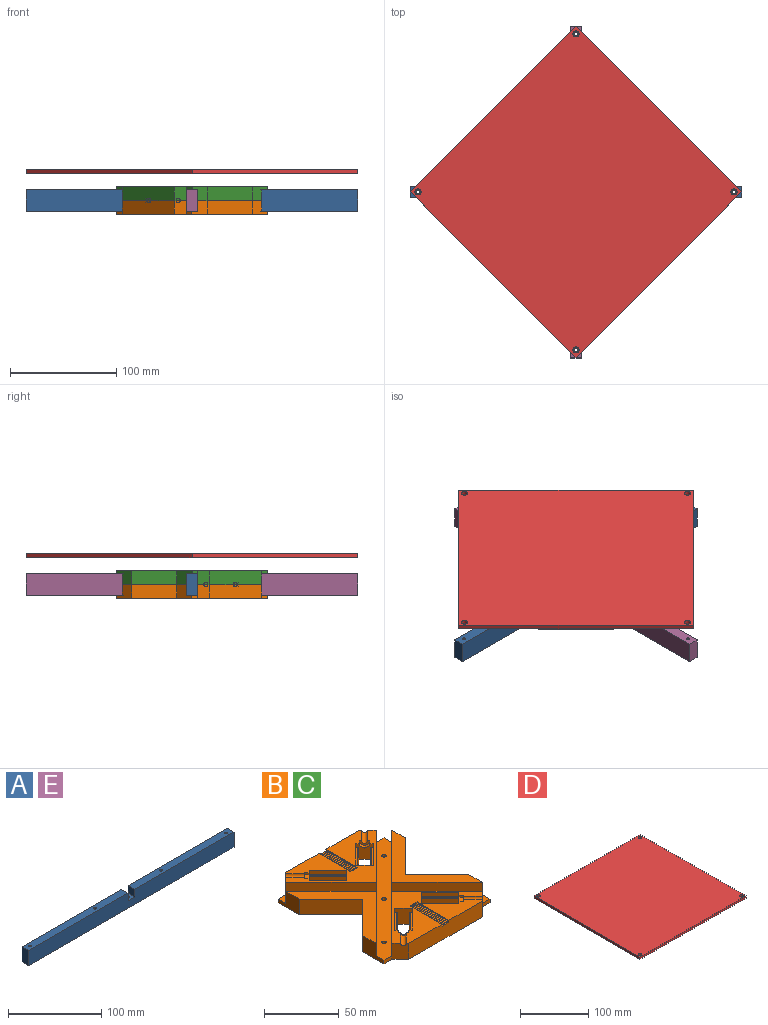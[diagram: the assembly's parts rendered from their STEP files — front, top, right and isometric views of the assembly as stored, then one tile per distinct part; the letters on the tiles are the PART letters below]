
ASSEMBLY  parts=5 mates=6
PART A: 15 faces, bbox 312x10x20 mm
  f0: plane 151x10mm, normal (0,0,1), area 1495.9mm2, adj f2,f3,f4,f7,f10,f14
  f1: cylinder r=1.5mm len=10mm, axis (0,0,-1), area 94.2mm2, adj f9,f12
  f2: plane 312x20mm, normal (0,-1,0), area 6140mm2, adj f0,f3,f5,f8,f9,f10,f11,f12
  f3: plane 20x10mm, normal (1,0,0), area 200mm2, adj f0,f2,f4,f9
  f4: plane 312x20mm, normal (0,1,0), area 6140mm2, adj f0,f3,f5,f8,f9,f10,f11,f12
  f5: plane 20x10mm, normal (-1,0,0), area 200mm2, adj f2,f4,f8,f9
  f6: cylinder r=1.5mm len=20mm, axis (0,0,-1), area 188.5mm2, adj f8,f9
  f7: cylinder r=1.5mm len=20mm, axis (0,0,-1), area 188.5mm2, adj f0,f9
  f8: plane 151x10mm, normal (0,0,1), area 1495.9mm2, adj f2,f4,f5,f6,f11,f13
  f9: plane 312x10mm, normal (0,0,-1), area 3084.7mm2, adj f1,f2,f3,f4,f5,f6,f7,f13
  f10: plane 10x10mm, normal (-1,0,0), area 100mm2, adj f0,f2,f4,f12
  f11: plane 10x10mm, normal (1,0,0), area 100mm2, adj f2,f4,f8,f12
  f12: plane 10x10mm, normal (0,0,1), area 92.9mm2, adj f1,f2,f4,f10,f11
  f13: cylinder r=1.5mm len=20mm, axis (0,0,1), area 188.5mm2, adj f8,f9
  f14: cylinder r=1.5mm len=20mm, axis (0,0,1), area 188.5mm2, adj f0,f9
PART B: 227 faces, bbox 100x116x13 mm
  f0: plane 6.5x0.5mm, normal (0,0,1), area 3.3mm2, adj f106,f107,f108,f198
  f1: plane 69.29x13mm, normal (0,1,0), area 890.7mm2, adj f5,f17,f48,f49,f106,f107,f154
  f2: plane 6.5x0.5mm, normal (0,0,1), area 3.3mm2, adj f103,f104,f105,f213
  f3: plane 69.29x13mm, normal (0,-1,0), area 890.7mm2, adj f4,f17,f46,f47,f103,f105,f110
  f4: plane 85.29x50.65mm, normal (0,0,1), area 1500.1mm2, adj f3,f6,f40,f41,f46,f47,f50,f51
  f5: plane 85.29x50.65mm, normal (0,0,1), area 1500.1mm2, adj f1,f7,f8,f38,f39,f48,f49,f53
  f6: plane 13x8.49mm, normal (0.71,0.71,0), area 95.6mm2, adj f4,f9,f10,f17,f67,f68,f69,f70
  f7: plane 13x8.49mm, normal (0.71,-0.71,0), area 95.6mm2, adj f5,f15,f16,f17,f55,f56,f57,f58
  f8: plane 13x8.49mm, normal (-0.71,-0.71,0), area 95.6mm2, adj f5,f13,f14,f17,f59,f60,f61,f62
  f9: plane 17.68x17.68mm, normal (0.71,-0.71,0), area 240mm2, adj f6,f17,f50,f95
  f10: plane 17.68x17.68mm, normal (-0.71,0.71,0), area 240mm2, adj f6,f17,f50,f96
  f11: plane 17.68x17.68mm, normal (-0.71,-0.71,0), area 240mm2, adj f17,f51,f52,f97
  f12: plane 17.68x17.68mm, normal (0.71,0.71,0), area 240mm2, adj f17,f51,f52,f98
  f13: plane 17.68x17.68mm, normal (-0.71,0.71,0), area 240mm2, adj f8,f17,f53,f99
  f14: plane 17.68x17.68mm, normal (0.71,-0.71,0), area 240mm2, adj f8,f17,f53,f100
  f15: plane 17.68x17.68mm, normal (0.71,0.71,0), area 240mm2, adj f7,f17,f54,f101
  f16: plane 17.68x17.68mm, normal (-0.71,-0.71,0), area 240mm2, adj f7,f17,f54,f102
  f17: plane 116x100mm, normal (0,0,-1), area 8601.3mm2, adj f1,f3,f6,f7,f8,f9,f10,f11
  f18: plane 20x13mm, normal (1,0,0), area 186.5mm2, adj f17,f21,f23,f36,f37,f43
  f19: plane 20x13mm, normal (-1,0,0), area 186.5mm2, adj f17,f20,f23,f28,f33,f45
  f20: plane 85.29x42.65mm, normal (0,0,1), area 918.7mm2, adj f19,f26,f33,f34,f44,f45
  f21: plane 7.35x3mm, normal (0,-1,0), area 22.1mm2, adj f17,f18,f23,f46
  f22: plane 7.35x3mm, normal (0,1,0), area 22.1mm2, adj f17,f23,f24,f48
  f23: plane 100x100mm, normal (0,0,1), area 2689.9mm2, adj f18,f19,f21,f22,f24,f25,f26,f27
  f24: plane 20x13mm, normal (1,0,0), area 186.5mm2, adj f17,f22,f23,f35,f37,f42
  f25: plane 7.35x3mm, normal (0,1,0), area 22.1mm2, adj f17,f23,f26,f49
  f26: plane 20x13mm, normal (-1,0,0), area 186.5mm2, adj f17,f20,f23,f25,f34,f44
  f27: cylinder r=1.5mm len=3mm, axis (0,0,-1), area 28.3mm2, adj f17,f23
  f28: plane 7.35x3mm, normal (0,-1,0), area 22.1mm2, adj f17,f19,f23,f47
  f29: cylinder r=1.5mm len=3mm, axis (0,0,-1), area 28.3mm2, adj f17,f23
  f30: cylinder r=1.5mm len=3mm, axis (0,0,-1), area 28.3mm2, adj f17,f23
  f31: cylinder r=1.5mm len=3mm, axis (0,0,-1), area 28.3mm2, adj f17,f23
  f32: cylinder r=1.5mm len=3mm, axis (0,0,-1), area 28.3mm2, adj f17,f23
  f33: plane 42.65x42.65mm, normal (0.71,-0.71,0), area 603.1mm2, adj f19,f20,f23,f34
  f34: plane 42.65x42.65mm, normal (0.71,0.71,0), area 603.1mm2, adj f20,f23,f26,f33
  f35: plane 42.65x42.65mm, normal (-0.71,0.71,0), area 603.1mm2, adj f23,f24,f36,f37
  f36: plane 42.65x42.65mm, normal (-0.71,-0.71,0), area 603.1mm2, adj f18,f23,f35,f37
  f37: plane 85.29x42.65mm, normal (0,0,1), area 918.7mm2, adj f18,f24,f35,f36,f42,f43
  f38: plane 42.65x42.65mm, normal (-0.71,-0.71,0), area 603.1mm2, adj f5,f23,f39,f49
  f39: plane 42.65x42.65mm, normal (0.71,-0.71,0), area 603.1mm2, adj f5,f23,f38,f48
  f40: plane 42.65x42.65mm, normal (0.71,0.71,0), area 603.1mm2, adj f4,f23,f41,f46
  f41: plane 42.65x42.65mm, normal (-0.71,0.71,0), area 603.1mm2, adj f4,f23,f40,f47
  f42: plane 30x30mm, normal (0.71,-0.71,0), area 551.5mm2, adj f17,f24,f37,f43
  f43: plane 30x30mm, normal (0.71,0.71,0), area 551.5mm2, adj f17,f18,f37,f42
  f44: plane 30x30mm, normal (-0.71,-0.71,0), area 551.5mm2, adj f17,f20,f26,f45
  f45: plane 30x30mm, normal (-0.71,0.71,0), area 551.5mm2, adj f17,f19,f20,f44
  f46: plane 13x8mm, normal (0.71,-0.71,0), area 140.8mm2, adj f3,f4,f17,f21,f40,f94
  f47: plane 13x8mm, normal (-0.71,-0.71,0), area 140.8mm2, adj f3,f4,f17,f28,f41,f93
  f48: plane 13x8mm, normal (0.71,0.71,0), area 140.8mm2, adj f1,f5,f17,f22,f39,f91
  f49: plane 13x8mm, normal (-0.71,0.71,0), area 140.8mm2, adj f1,f5,f17,f25,f38,f92
  f50: plane 13x8.49mm, normal (-0.71,-0.71,0), area 116.1mm2, adj f4,f9,f10,f17,f67,f68,f69,f70
  f51: plane 13x8.49mm, normal (0.71,-0.71,0), area 116.1mm2, adj f4,f11,f12,f17,f63,f64,f65,f66
  f52: plane 13x8.49mm, normal (-0.71,0.71,0), area 95.6mm2, adj f4,f11,f12,f17,f63,f64,f65,f66
  f53: plane 13x8.49mm, normal (0.71,0.71,0), area 116.1mm2, adj f5,f13,f14,f17,f59,f60,f61,f62
  f54: plane 13x8.49mm, normal (-0.71,0.71,0), area 116.1mm2, adj f5,f15,f16,f17,f55,f56,f57,f58
  f55: plane 18.81x18.81mm, normal (0,0,1), area 40mm2, adj f7,f54,f56,f102
  f56: plane 17.68x17.68mm, normal (-0.71,-0.71,0), area 75mm2, adj f5,f7,f54,f55
  f57: plane 18.81x18.81mm, normal (0,0,1), area 40mm2, adj f7,f54,f58,f101
  f58: plane 17.68x17.68mm, normal (0.71,0.71,0), area 75mm2, adj f5,f7,f54,f57
  f59: plane 18.81x18.81mm, normal (0,0,1), area 40mm2, adj f8,f53,f60,f100
  f60: plane 17.68x17.68mm, normal (0.71,-0.71,0), area 75mm2, adj f5,f8,f53,f59
  f61: plane 18.81x18.81mm, normal (0,0,1), area 40mm2, adj f8,f53,f62,f99
  f62: plane 17.68x17.68mm, normal (-0.71,0.71,0), area 75mm2, adj f5,f8,f53,f61
  f63: plane 18.81x18.81mm, normal (0,0,1), area 40mm2, adj f51,f52,f64,f98
  f64: plane 17.68x17.68mm, normal (0.71,0.71,0), area 75mm2, adj f4,f51,f52,f63
  f65: plane 18.81x18.81mm, normal (0,0,1), area 40mm2, adj f51,f52,f66,f97
  f66: plane 17.68x17.68mm, normal (-0.71,-0.71,0), area 75mm2, adj f4,f51,f52,f65
  f67: plane 18.81x18.81mm, normal (0,0,1), area 40mm2, adj f6,f50,f68,f96
  f68: plane 17.68x17.68mm, normal (-0.71,0.71,0), area 75mm2, adj f4,f6,f50,f67
  f69: plane 18.81x18.81mm, normal (0,0,1), area 40mm2, adj f6,f50,f70,f95
  f70: plane 17.68x17.68mm, normal (0.71,-0.71,0), area 75mm2, adj f4,f6,f50,f69
  f71: plane 2.19x2.19mm, normal (0.71,-0.71,0), area 6.2mm2, adj f5,f8,f72,f75
  f72: plane 4.62x4.62mm, normal (0.35,-0.35,0.87), area 12.3mm2, adj f8,f71,f73,f75
  f73: plane 4.62x4.62mm, normal (-0.35,0.35,0.87), area 12.3mm2, adj f8,f72,f74,f75
  f74: plane 2.19x2.19mm, normal (-0.71,0.71,0), area 6.2mm2, adj f5,f8,f73,f75
  f75: plane 4.87x4.87mm, normal (-0.71,-0.71,0), area 14.2mm2, adj f5,f71,f72,f73,f74,f91
  f76: plane 2.19x2.19mm, normal (0.71,0.71,0), area 6.2mm2, adj f5,f7,f77,f80
  f77: plane 4.62x4.62mm, normal (0.35,0.35,0.87), area 12.3mm2, adj f7,f76,f78,f80
  f78: plane 4.62x4.62mm, normal (-0.35,-0.35,0.87), area 12.3mm2, adj f7,f77,f79,f80
  f79: plane 2.19x2.19mm, normal (-0.71,-0.71,0), area 6.2mm2, adj f5,f7,f78,f80
  f80: plane 4.87x4.87mm, normal (0.71,-0.71,0), area 14.2mm2, adj f5,f76,f77,f78,f79,f92
  f81: plane 2.19x2.19mm, normal (-0.71,0.71,0), area 6.2mm2, adj f4,f6,f82,f85
  f82: plane 4.62x4.62mm, normal (-0.35,0.35,0.87), area 12.3mm2, adj f6,f81,f83,f85
  f83: plane 4.62x4.62mm, normal (0.35,-0.35,0.87), area 12.3mm2, adj f6,f82,f84,f85
  f84: plane 2.19x2.19mm, normal (0.71,-0.71,0), area 6.2mm2, adj f4,f6,f83,f85
  f85: plane 4.87x4.87mm, normal (0.71,0.71,0), area 14.2mm2, adj f4,f81,f82,f83,f84,f93
  f86: plane 2.19x2.19mm, normal (-0.71,-0.71,0), area 6.2mm2, adj f4,f52,f87,f90
  f87: plane 4.62x4.62mm, normal (-0.35,-0.35,0.87), area 12.3mm2, adj f52,f86,f88,f90
  f88: plane 4.62x4.62mm, normal (0.35,0.35,0.87), area 12.3mm2, adj f52,f87,f89,f90
  f89: plane 2.19x2.19mm, normal (0.71,0.71,0), area 6.2mm2, adj f4,f52,f88,f90
  f90: plane 4.87x4.87mm, normal (-0.71,0.71,0), area 14.2mm2, adj f4,f86,f87,f88,f89,f94
  f91: cylinder r=2mm len=11.6mm, axis (-0.71,-0.71,0), area 78mm2, adj f5,f48,f75
  f92: cylinder r=2mm len=11.6mm, axis (0.71,-0.71,0), area 78mm2, adj f5,f49,f80
  f93: cylinder r=2mm len=11.6mm, axis (0.71,0.71,0), area 78mm2, adj f4,f47,f85
  f94: cylinder r=2mm len=11.6mm, axis (-0.71,0.71,0), area 78mm2, adj f4,f46,f90
  f95: cylinder r=0.4mm len=17.96mm, axis (-0.71,-0.71,0), area 15.7mm2, adj f6,f9,f50,f69
  f96: cylinder r=0.4mm len=17.96mm, axis (0.71,0.71,0), area 15.7mm2, adj f6,f10,f50,f67
  f97: cylinder r=0.4mm len=17.96mm, axis (-0.71,0.71,0), area 15.7mm2, adj f11,f51,f52,f65
  f98: cylinder r=0.4mm len=17.96mm, axis (0.71,-0.71,0), area 15.7mm2, adj f12,f51,f52,f63
  f99: cylinder r=0.4mm len=17.96mm, axis (0.71,0.71,0), area 15.7mm2, adj f8,f13,f53,f61
  f100: cylinder r=0.4mm len=17.96mm, axis (-0.71,-0.71,0), area 15.7mm2, adj f8,f14,f53,f59
  f101: cylinder r=0.4mm len=17.96mm, axis (0.71,-0.71,0), area 15.7mm2, adj f7,f15,f54,f57
  f102: cylinder r=0.4mm len=17.96mm, axis (-0.71,0.71,0), area 15.7mm2, adj f7,f16,f54,f55
  f103: plane 30x1.55mm, normal (-1,0,0), area 30.1mm2, adj f2,f3,f4,f104,f109,f110,f111,f112
  f104: plane 6.5x0.35mm, normal (0,-1,0), area 2.3mm2, adj f2,f4,f103,f105
  f105: plane 30x1.55mm, normal (1,0,0), area 30.1mm2, adj f2,f3,f4,f104,f109,f110,f111,f112
  f106: plane 30x1.55mm, normal (-1,0,0), area 30.1mm2, adj f0,f1,f5,f108,f153,f154,f155,f156
  f107: plane 30x1.55mm, normal (1,0,0), area 30.1mm2, adj f0,f1,f5,f108,f153,f154,f155,f156
  f108: plane 6.5x0.35mm, normal (0,1,0), area 2.3mm2, adj f0,f5,f106,f107
  f109: plane 6.5x0.7mm, normal (0,-1,0), area 4.5mm2, adj f103,f105,f110,f226
  f110: plane 6.5x1mm, normal (0,0,1), area 6.5mm2, adj f3,f103,f105,f109
  f111: plane 6.5x0.7mm, normal (0,-1,0), area 4.5mm2, adj f103,f105,f113,f213
  f112: plane 6.5x0.7mm, normal (0,1,0), area 4.5mm2, adj f103,f105,f113,f212
  f113: plane 6.5x1mm, normal (0,0,1), area 6.5mm2, adj f103,f105,f111,f112
  f114: plane 6.5x0.7mm, normal (0,-1,0), area 4.5mm2, adj f103,f105,f116,f212
  f115: plane 6.5x0.7mm, normal (0,1,0), area 4.5mm2, adj f103,f105,f116,f214
  f116: plane 6.5x1mm, normal (0,0,1), area 6.5mm2, adj f103,f105,f114,f115
  f117: plane 6.5x0.7mm, normal (0,-1,0), area 4.5mm2, adj f103,f105,f119,f214
  f118: plane 6.5x0.7mm, normal (0,1,0), area 4.5mm2, adj f103,f105,f119,f215
  f119: plane 6.5x1mm, normal (0,0,1), area 6.5mm2, adj f103,f105,f117,f118
  f120: plane 6.5x0.7mm, normal (0,-1,0), area 4.5mm2, adj f103,f105,f122,f215
  f121: plane 6.5x0.7mm, normal (0,1,0), area 4.5mm2, adj f103,f105,f122,f216
  f122: plane 6.5x1mm, normal (0,0,1), area 6.5mm2, adj f103,f105,f120,f121
  f123: plane 6.5x0.7mm, normal (0,-1,0), area 4.5mm2, adj f103,f105,f125,f216
  f124: plane 6.5x0.7mm, normal (0,1,0), area 4.5mm2, adj f103,f105,f125,f217
  f125: plane 6.5x1mm, normal (0,0,1), area 6.5mm2, adj f103,f105,f123,f124
  f126: plane 6.5x0.7mm, normal (0,-1,0), area 4.5mm2, adj f103,f105,f128,f217
  f127: plane 6.5x0.7mm, normal (0,1,0), area 4.5mm2, adj f103,f105,f128,f218
  f128: plane 6.5x1mm, normal (0,0,1), area 6.5mm2, adj f103,f105,f126,f127
  f129: plane 6.5x0.7mm, normal (0,-1,0), area 4.5mm2, adj f103,f105,f131,f218
  f130: plane 6.5x0.7mm, normal (0,1,0), area 4.5mm2, adj f103,f105,f131,f219
  f131: plane 6.5x1mm, normal (0,0,1), area 6.5mm2, adj f103,f105,f129,f130
  f132: plane 6.5x0.7mm, normal (0,-1,0), area 4.5mm2, adj f103,f105,f134,f219
  f133: plane 6.5x0.7mm, normal (0,1,0), area 4.5mm2, adj f103,f105,f134,f220
  f134: plane 6.5x1mm, normal (0,0,1), area 6.5mm2, adj f103,f105,f132,f133
  f135: plane 6.5x0.7mm, normal (0,-1,0), area 4.5mm2, adj f103,f105,f137,f220
  f136: plane 6.5x0.7mm, normal (0,1,0), area 4.5mm2, adj f103,f105,f137,f221
  f137: plane 6.5x1mm, normal (0,0,1), area 6.5mm2, adj f103,f105,f135,f136
  f138: plane 6.5x0.7mm, normal (0,-1,0), area 4.5mm2, adj f103,f105,f140,f221
  f139: plane 6.5x0.7mm, normal (0,1,0), area 4.5mm2, adj f103,f105,f140,f222
  f140: plane 6.5x1mm, normal (0,0,1), area 6.5mm2, adj f103,f105,f138,f139
  f141: plane 6.5x0.7mm, normal (0,-1,0), area 4.5mm2, adj f103,f105,f143,f222
  f142: plane 6.5x0.7mm, normal (0,1,0), area 4.5mm2, adj f103,f105,f143,f223
  f143: plane 6.5x1mm, normal (0,0,1), area 6.5mm2, adj f103,f105,f141,f142
  f144: plane 6.5x0.7mm, normal (0,-1,0), area 4.5mm2, adj f103,f105,f146,f223
  f145: plane 6.5x0.7mm, normal (0,1,0), area 4.5mm2, adj f103,f105,f146,f224
  f146: plane 6.5x1mm, normal (0,0,1), area 6.5mm2, adj f103,f105,f144,f145
  f147: plane 6.5x0.7mm, normal (0,-1,0), area 4.5mm2, adj f103,f105,f149,f224
  f148: plane 6.5x0.7mm, normal (0,1,0), area 4.5mm2, adj f103,f105,f149,f225
  f149: plane 6.5x1mm, normal (0,0,1), area 6.5mm2, adj f103,f105,f147,f148
  f150: plane 6.5x0.7mm, normal (0,-1,0), area 4.5mm2, adj f103,f105,f152,f225
  f151: plane 6.5x0.7mm, normal (0,1,0), area 4.5mm2, adj f103,f105,f152,f226
  f152: plane 6.5x1mm, normal (0,0,1), area 6.5mm2, adj f103,f105,f150,f151
  f153: plane 6.5x0.7mm, normal (0,1,0), area 4.5mm2, adj f106,f107,f154,f211
  f154: plane 6.5x1mm, normal (0,0,1), area 6.5mm2, adj f1,f106,f107,f153
  f155: plane 6.5x0.7mm, normal (0,-1,0), area 4.5mm2, adj f106,f107,f157,f197
  f156: plane 6.5x0.7mm, normal (0,1,0), area 4.5mm2, adj f106,f107,f157,f198
  f157: plane 6.5x1mm, normal (0,0,1), area 6.5mm2, adj f106,f107,f155,f156
  f158: plane 6.5x0.7mm, normal (0,-1,0), area 4.5mm2, adj f106,f107,f160,f199
  f159: plane 6.5x0.7mm, normal (0,1,0), area 4.5mm2, adj f106,f107,f160,f197
  f160: plane 6.5x1mm, normal (0,0,1), area 6.5mm2, adj f106,f107,f158,f159
  f161: plane 6.5x0.7mm, normal (0,-1,0), area 4.5mm2, adj f106,f107,f163,f200
  f162: plane 6.5x0.7mm, normal (0,1,0), area 4.5mm2, adj f106,f107,f163,f199
  f163: plane 6.5x1mm, normal (0,0,1), area 6.5mm2, adj f106,f107,f161,f162
  f164: plane 6.5x0.7mm, normal (0,-1,0), area 4.5mm2, adj f106,f107,f166,f201
  f165: plane 6.5x0.7mm, normal (0,1,0), area 4.5mm2, adj f106,f107,f166,f200
  f166: plane 6.5x1mm, normal (0,0,1), area 6.5mm2, adj f106,f107,f164,f165
  f167: plane 6.5x0.7mm, normal (0,-1,0), area 4.5mm2, adj f106,f107,f169,f202
  f168: plane 6.5x0.7mm, normal (0,1,0), area 4.5mm2, adj f106,f107,f169,f201
  f169: plane 6.5x1mm, normal (0,0,1), area 6.5mm2, adj f106,f107,f167,f168
  f170: plane 6.5x0.7mm, normal (0,-1,0), area 4.5mm2, adj f106,f107,f172,f203
  f171: plane 6.5x0.7mm, normal (0,1,0), area 4.5mm2, adj f106,f107,f172,f202
  f172: plane 6.5x1mm, normal (0,0,1), area 6.5mm2, adj f106,f107,f170,f171
  f173: plane 6.5x0.7mm, normal (0,-1,0), area 4.5mm2, adj f106,f107,f175,f204
  f174: plane 6.5x0.7mm, normal (0,1,0), area 4.5mm2, adj f106,f107,f175,f203
  f175: plane 6.5x1mm, normal (0,0,1), area 6.5mm2, adj f106,f107,f173,f174
  f176: plane 6.5x0.7mm, normal (0,-1,0), area 4.5mm2, adj f106,f107,f178,f205
  f177: plane 6.5x0.7mm, normal (0,1,0), area 4.5mm2, adj f106,f107,f178,f204
  f178: plane 6.5x1mm, normal (0,0,1), area 6.5mm2, adj f106,f107,f176,f177
  f179: plane 6.5x0.7mm, normal (0,-1,0), area 4.5mm2, adj f106,f107,f181,f206
  f180: plane 6.5x0.7mm, normal (0,1,0), area 4.5mm2, adj f106,f107,f181,f205
  f181: plane 6.5x1mm, normal (0,0,1), area 6.5mm2, adj f106,f107,f179,f180
  f182: plane 6.5x0.7mm, normal (0,-1,0), area 4.5mm2, adj f106,f107,f184,f207
  f183: plane 6.5x0.7mm, normal (0,1,0), area 4.5mm2, adj f106,f107,f184,f206
  f184: plane 6.5x1mm, normal (0,0,1), area 6.5mm2, adj f106,f107,f182,f183
  f185: plane 6.5x0.7mm, normal (0,-1,0), area 4.5mm2, adj f106,f107,f187,f208
  f186: plane 6.5x0.7mm, normal (0,1,0), area 4.5mm2, adj f106,f107,f187,f207
  f187: plane 6.5x1mm, normal (0,0,1), area 6.5mm2, adj f106,f107,f185,f186
  f188: plane 6.5x0.7mm, normal (0,-1,0), area 4.5mm2, adj f106,f107,f190,f209
  f189: plane 6.5x0.7mm, normal (0,1,0), area 4.5mm2, adj f106,f107,f190,f208
  f190: plane 6.5x1mm, normal (0,0,1), area 6.5mm2, adj f106,f107,f188,f189
  f191: plane 6.5x0.7mm, normal (0,-1,0), area 4.5mm2, adj f106,f107,f193,f210
  f192: plane 6.5x0.7mm, normal (0,1,0), area 4.5mm2, adj f106,f107,f193,f209
  f193: plane 6.5x1mm, normal (0,0,1), area 6.5mm2, adj f106,f107,f191,f192
  f194: plane 6.5x0.7mm, normal (0,-1,0), area 4.5mm2, adj f106,f107,f196,f211
  f195: plane 6.5x0.7mm, normal (0,1,0), area 4.5mm2, adj f106,f107,f196,f210
  f196: plane 6.5x1mm, normal (0,0,1), area 6.5mm2, adj f106,f107,f194,f195
  f197: cylinder r=0.5mm len=6.5mm, axis (-1,0,0), area 10.2mm2, adj f106,f107,f155,f159
  f198: cylinder r=0.5mm len=6.5mm, axis (-1,0,0), area 5.1mm2, adj f0,f106,f107,f156
  f199: cylinder r=0.5mm len=6.5mm, axis (-1,0,0), area 10.2mm2, adj f106,f107,f158,f162
  f200: cylinder r=0.5mm len=6.5mm, axis (-1,0,0), area 10.2mm2, adj f106,f107,f161,f165
  f201: cylinder r=0.5mm len=6.5mm, axis (-1,0,0), area 10.2mm2, adj f106,f107,f164,f168
  f202: cylinder r=0.5mm len=6.5mm, axis (-1,0,0), area 10.2mm2, adj f106,f107,f167,f171
  f203: cylinder r=0.5mm len=6.5mm, axis (-1,0,0), area 10.2mm2, adj f106,f107,f170,f174
  f204: cylinder r=0.5mm len=6.5mm, axis (-1,0,0), area 10.2mm2, adj f106,f107,f173,f177
  f205: cylinder r=0.5mm len=6.5mm, axis (-1,0,0), area 10.2mm2, adj f106,f107,f176,f180
  f206: cylinder r=0.5mm len=6.5mm, axis (-1,0,0), area 10.2mm2, adj f106,f107,f179,f183
  f207: cylinder r=0.5mm len=6.5mm, axis (-1,0,0), area 10.2mm2, adj f106,f107,f182,f186
  f208: cylinder r=0.5mm len=6.5mm, axis (-1,0,0), area 10.2mm2, adj f106,f107,f185,f189
  f209: cylinder r=0.5mm len=6.5mm, axis (-1,0,0), area 10.2mm2, adj f106,f107,f188,f192
  f210: cylinder r=0.5mm len=6.5mm, axis (-1,0,0), area 10.2mm2, adj f106,f107,f191,f195
  f211: cylinder r=0.5mm len=6.5mm, axis (-1,0,0), area 10.2mm2, adj f106,f107,f153,f194
  f212: cylinder r=0.5mm len=6.5mm, axis (1,0,0), area 10.2mm2, adj f103,f105,f112,f114
  f213: cylinder r=0.5mm len=6.5mm, axis (1,0,0), area 5.1mm2, adj f2,f103,f105,f111
  f214: cylinder r=0.5mm len=6.5mm, axis (1,0,0), area 10.2mm2, adj f103,f105,f115,f117
  f215: cylinder r=0.5mm len=6.5mm, axis (1,0,0), area 10.2mm2, adj f103,f105,f118,f120
  f216: cylinder r=0.5mm len=6.5mm, axis (1,0,0), area 10.2mm2, adj f103,f105,f121,f123
  f217: cylinder r=0.5mm len=6.5mm, axis (1,0,0), area 10.2mm2, adj f103,f105,f124,f126
  f218: cylinder r=0.5mm len=6.5mm, axis (1,0,0), area 10.2mm2, adj f103,f105,f127,f129
  f219: cylinder r=0.5mm len=6.5mm, axis (1,0,0), area 10.2mm2, adj f103,f105,f130,f132
  f220: cylinder r=0.5mm len=6.5mm, axis (1,0,0), area 10.2mm2, adj f103,f105,f133,f135
  f221: cylinder r=0.5mm len=6.5mm, axis (1,0,0), area 10.2mm2, adj f103,f105,f136,f138
  f222: cylinder r=0.5mm len=6.5mm, axis (1,0,0), area 10.2mm2, adj f103,f105,f139,f141
  f223: cylinder r=0.5mm len=6.5mm, axis (1,0,0), area 10.2mm2, adj f103,f105,f142,f144
  f224: cylinder r=0.5mm len=6.5mm, axis (1,0,0), area 10.2mm2, adj f103,f105,f145,f147
  f225: cylinder r=0.5mm len=6.5mm, axis (1,0,0), area 10.2mm2, adj f103,f105,f148,f150
  f226: cylinder r=0.5mm len=6.5mm, axis (1,0,0), area 10.2mm2, adj f103,f105,f109,f151
PART C: same geometry as B
PART D: 10 faces, bbox 220x220x4 mm
  f0: plane 220x4mm, normal (1,0,0), area 880mm2, adj f1,f6,f8,f9
  f1: plane 220x4mm, normal (0,1,0), area 880mm2, adj f0,f2,f8,f9
  f2: plane 220x4mm, normal (-1,0,0), area 880mm2, adj f1,f6,f8,f9
  f3: cylinder r=2.85mm len=5.7mm, axis (0,0,-1), area 71.6mm2, adj f8,f9
  f4: cylinder r=2.85mm len=5.7mm, axis (0,0,-1), area 71.6mm2, adj f8,f9
  f5: cylinder r=2.85mm len=5.7mm, axis (0,0,-1), area 71.6mm2, adj f8,f9
  f6: plane 220x4mm, normal (0,-1,0), area 880mm2, adj f0,f2,f8,f9
  f7: cylinder r=2.85mm len=5.7mm, axis (0,0,-1), area 71.6mm2, adj f8,f9
  f8: plane 220x220mm, normal (0,0,1), area 48297.9mm2, adj f0,f1,f2,f3,f4,f5,f6,f7
  f9: plane 220x220mm, normal (0,0,-1), area 48297.9mm2, adj f0,f1,f2,f3,f4,f5,f6,f7
PART E: same geometry as A
PLACE A at identity
PLACE B rot(axis=(0,0,-1),45deg) t=(0,0,-3)mm
PLACE C rot(axis=(0.92,-0.38,0),180deg) t=(0,0,23)mm
PLACE D rot(axis=(0,0,1),45deg) t=(0,-0.01,35)mm
PLACE E rot(axis=(0.71,0.71,0),180deg) t=(0,0,20)mm
MATE revolute C.f32 <-> A.f14  axis (0,0,-1) through (50,0,20)mm
MATE revolute D.f4 <-> E.f6  axis (0,0,-1) through (0,-148.5,35)mm
MATE fastened E.f1 <-> A.f1  axis (0,0,-1) through (0,0,10)mm
MATE revolute B.f31 <-> A.f14  axis (0,0,1) through (50,0,0)mm
MATE revolute B.f29 <-> A.f1  axis (0,0,1) through (0,0,0)mm
MATE revolute C.f29 <-> E.f1  axis (0,0,-1) through (0,0,20)mm
